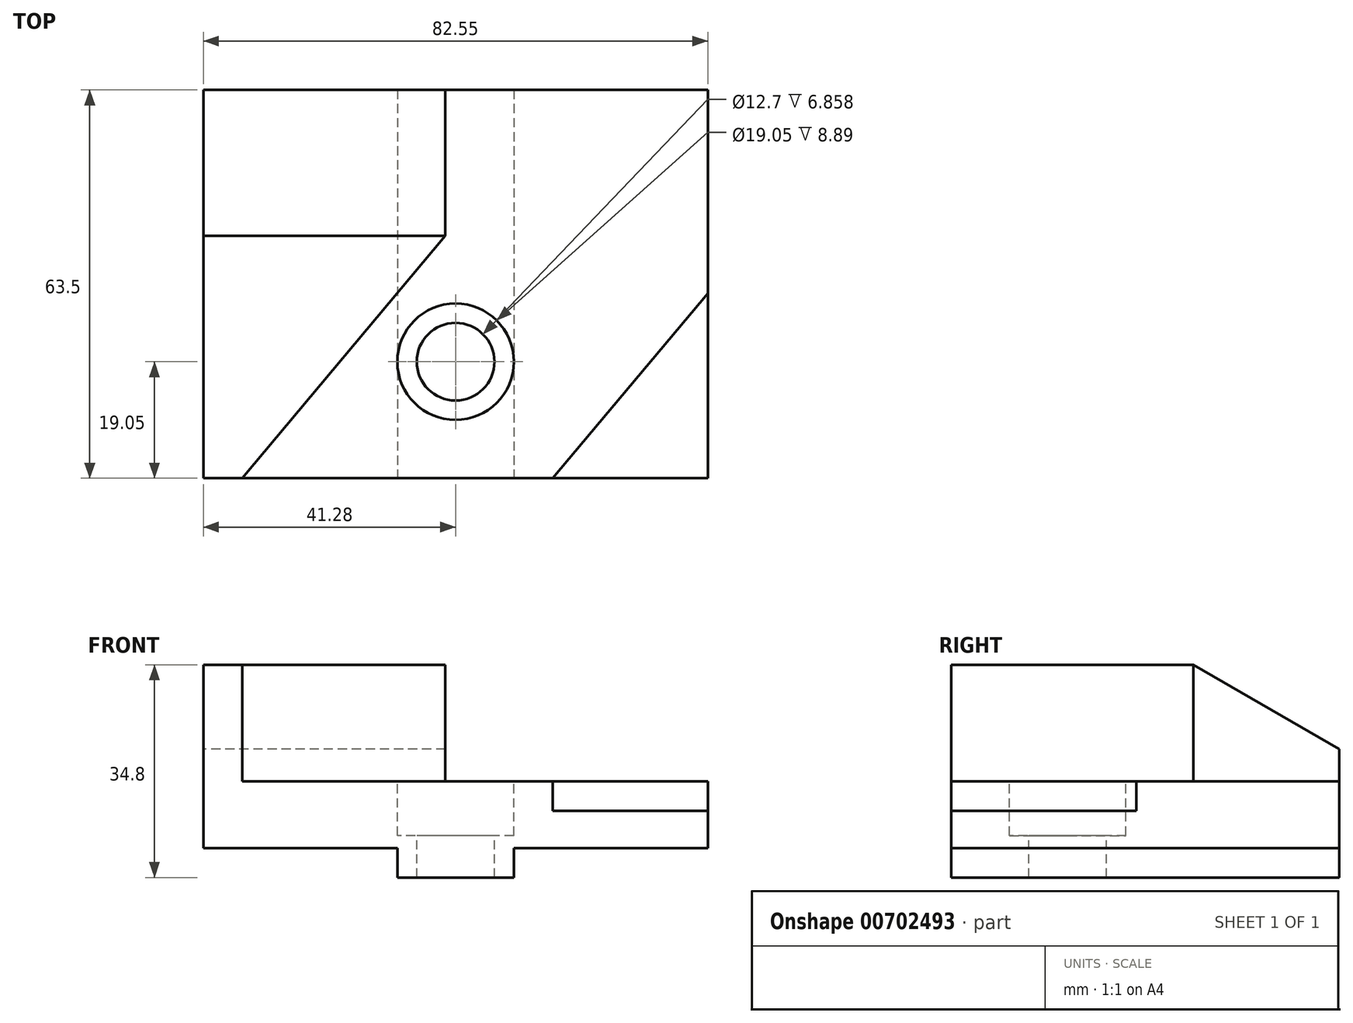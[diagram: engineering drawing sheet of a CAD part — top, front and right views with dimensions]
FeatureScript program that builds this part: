
annotation { "Feature Type Name" : "Feature", "Feature Type Description" : "" }
export const myFeature = defineFeature(function(context is Context, id is Id, definition is map)
    precondition{}
    {
        {
            var Q0;
            Q0=qCreatedBy(makeId("Front.planeOp"),FACE);
            var sketch = newSketch(context, id + "F0", { "sketchPlane" : qUnion([Q0])});
            skLineSegment(sketch, "E0.bottom", {"start": v(41.27, 17.4) * mm, "end": v(-41.28, 17.4) * mm});
            skLineSegment(sketch, "E0.top", {"start": v(41.28, -17.4) * mm, "end": v(-41.27, -17.4) * mm});
            skLineSegment(sketch, "E0.left", {"start": v(41.27, 17.4) * mm, "end": v(41.28, -17.4) * mm});
            skLineSegment(sketch, "E0.right", {"start": v(-41.28, 17.4) * mm, "end": v(-41.27, -17.4) * mm});
            skPoint(sketch, "E0.middle", {"position": v(0, 0) * mm});
            skSolve(sketch);
        }
        {
            var Q0;
            Q0=qSketchRegion(id+"F0",true);
            extrude(context, id + "F1", {"entities" : qUnion([Q0]), "depth" : 63.5 * mm});
        }
        {
            var Q0;
            Q0=makeQuery(id+"F1.opExtrude","CAP_FACE",FACE,{"disambiguationData":[OSD([sQuery(id+"F0.wireOp",EDGE,"E0.bottom"),sQuery(id+"F0.wireOp",EDGE,"E0.top"),sQuery(id+"F0.wireOp",EDGE,"E0.left"),sQuery(id+"F0.wireOp",EDGE,"E0.right")])],"isStart":false});
            var sketch = newSketch(context, id + "F2", { "sketchPlane" : qUnion([Q0])});
            skLineSegment(sketch, "E1.bottom", {"start": v(-41.27, -17.4) * mm, "end": v(-9.52, -17.4) * mm});
            skLineSegment(sketch, "E1.top", {"start": v(-41.27, -12.57) * mm, "end": v(-9.52, -12.57) * mm});
            skLineSegment(sketch, "E1.left", {"start": v(-41.27, -17.4) * mm, "end": v(-41.27, -12.57) * mm});
            skLineSegment(sketch, "E1.right", {"start": v(-9.52, -17.4) * mm, "end": v(-9.52, -12.57) * mm});
            skLineSegment(sketch, "E2.bottom", {"start": v(41.28, -17.4) * mm, "end": v(9.53, -17.4) * mm});
            skLineSegment(sketch, "E2.top", {"start": v(41.28, -12.57) * mm, "end": v(9.53, -12.57) * mm});
            skLineSegment(sketch, "E2.left", {"start": v(41.28, -17.4) * mm, "end": v(41.28, -12.57) * mm});
            skLineSegment(sketch, "E2.right", {"start": v(9.53, -17.4) * mm, "end": v(9.53, -12.57) * mm});
            skSolve(sketch);
        }
        {
            var Q0;
            Q0=qSketchRegion(id+"F2",true);
            extrude(context, id + "F3", {"entities" : qUnion([Q0]), "operationType" : NewBodyOperationType.REMOVE, "endBound" : BoundingType.THROUGH_ALL, "oppositeDirection" : true, "depth" : 25.4 * mm});
        }
        {
            var Q0;
            Q0=makeQuery(id+"F1.opExtrude","SWEPT_FACE",FACE,{"disambiguationData":[OSD([sQuery(id+"F0.wireOp",EDGE,"E0.bottom")])]});
            var sketch = newSketch(context, id + "F4", { "sketchPlane" : qUnion([Q0])});
            skLineSegment(sketch, "E3", {"start": v(-34.92, -63.5) * mm, "end": v(-1.68, -23.88) * mm});
            skLineSegment(sketch, "E4", {"start": v(-1.68, -23.88) * mm, "end": v(-1.68, 0) * mm});
            skLineSegment(sketch, "E5", {"start": v(-1.68, 0) * mm, "end": v(41.27, 0) * mm});
            skLineSegment(sketch, "E6", {"start": v(41.27, 0) * mm, "end": v(41.27, -63.5) * mm});
            skLineSegment(sketch, "E7", {"start": v(41.28, -63.5) * mm, "end": v(-34.92, -63.5) * mm});
            skSolve(sketch);
        }
        {
            var Q0;
            Q0=qSketchRegion(id+"F4",true);
            extrude(context, id + "F5", {"entities" : qUnion([Q0]), "operationType" : NewBodyOperationType.REMOVE, "oppositeDirection" : true, "depth" : 19.05 * mm});
        }
        {
            var Q0;
            Q0=makeQuery(id+"F1.opExtrude","SWEPT_FACE",FACE,{"disambiguationData":[OSD([sQuery(id+"F0.wireOp",EDGE,"E0.right")])]});
            var sketch = newSketch(context, id + "F6", { "sketchPlane" : qUnion([Q0])});
            skLineSegment(sketch, "E8", {"start": v(0, 3.61) * mm, "end": v(0, 17.4) * mm});
            skLineSegment(sketch, "E9", {"start": v(0, 17.4) * mm, "end": v(23.88, 17.4) * mm});
            skLineSegment(sketch, "E10", {"start": v(23.88, 17.4) * mm, "end": v(0, 3.61) * mm});
            skSolve(sketch);
        }
        {
            var Q0;
            Q0=qSketchRegion(id+"F6",true);
            extrude(context, id + "F7", {"entities" : qUnion([Q0]), "operationType" : NewBodyOperationType.REMOVE, "endBound" : BoundingType.THROUGH_ALL, "oppositeDirection" : true, "depth" : 25.4 * mm});
        }
        {
            var Q0;
            Q0=makeQuery(id+"F5.boolean.opBoolean","COPY",FACE,{"derivedFrom":makeQuery(id+"F5.opExtrude","CAP_FACE",FACE,{"disambiguationData":[OSD([sQuery(id+"F4.wireOp",EDGE,"E3"),sQuery(id+"F4.wireOp",EDGE,"E4"),sQuery(id+"F4.wireOp",EDGE,"E5"),sQuery(id+"F4.wireOp",EDGE,"E6"),sQuery(id+"F4.wireOp",EDGE,"E7")])],"isStart":false})});
            var sketch = newSketch(context, id + "F8", { "sketchPlane" : qUnion([Q0])});
            skLineSegment(sketch, "E11", {"start": v(41.27, -63.5) * mm, "end": v(15.87, -63.5) * mm});
            skLineSegment(sketch, "E12", {"start": v(15.87, -63.5) * mm, "end": v(41.27, -33.23) * mm});
            skLineSegment(sketch, "E13", {"start": v(41.27, -33.23) * mm, "end": v(41.27, -63.5) * mm});
            skSolve(sketch);
        }
        {
            var Q0;
            Q0=qSketchRegion(id+"F8",true);
            extrude(context, id + "F9", {"entities" : qUnion([Q0]), "operationType" : NewBodyOperationType.REMOVE, "oppositeDirection" : true, "depth" : 4.83 * mm});
        }
        {
            var Q0;
            Q0=makeQuery(id+"F5.boolean.opBoolean","COPY",FACE,{"derivedFrom":makeQuery(id+"F5.opExtrude","CAP_FACE",FACE,{"disambiguationData":[OSD([sQuery(id+"F4.wireOp",EDGE,"E3"),sQuery(id+"F4.wireOp",EDGE,"E4"),sQuery(id+"F4.wireOp",EDGE,"E5"),sQuery(id+"F4.wireOp",EDGE,"E6"),sQuery(id+"F4.wireOp",EDGE,"E7")])],"isStart":false})});
            var sketch = newSketch(context, id + "F10", { "sketchPlane" : qUnion([Q0])});
            skCircle(sketch, "E14", {"center": v(0, -44.45) * mm, "radius": 6.35 * mm});
            skSolve(sketch);
        }
        {
            var Q0;
            Q0=qSketchRegion(id+"F10",true);
            extrude(context, id + "F11", {"entities" : qUnion([Q0]), "operationType" : NewBodyOperationType.REMOVE, "endBound" : BoundingType.THROUGH_ALL, "oppositeDirection" : true, "depth" : 25.4 * mm});
        }
        {
            var Q0;
            Q0=makeQuery(id+"F5.boolean.opBoolean","COPY",FACE,{"derivedFrom":makeQuery(id+"F5.opExtrude","CAP_FACE",FACE,{"disambiguationData":[OSD([sQuery(id+"F4.wireOp",EDGE,"E3"),sQuery(id+"F4.wireOp",EDGE,"E4"),sQuery(id+"F4.wireOp",EDGE,"E5"),sQuery(id+"F4.wireOp",EDGE,"E6"),sQuery(id+"F4.wireOp",EDGE,"E7")])],"isStart":false})});
            var sketch = newSketch(context, id + "F12", { "sketchPlane" : qUnion([Q0])});
            skCircle(sketch, "E15", {"center": v(0, -44.45) * mm, "radius": 9.53 * mm});
            skSolve(sketch);
        }
        {
            var Q0;
            Q0=qSketchRegion(id+"F12",true);
            extrude(context, id + "F13", {"entities" : qUnion([Q0]), "operationType" : NewBodyOperationType.REMOVE, "oppositeDirection" : true, "depth" : 8.9 * mm});
        }
    });
